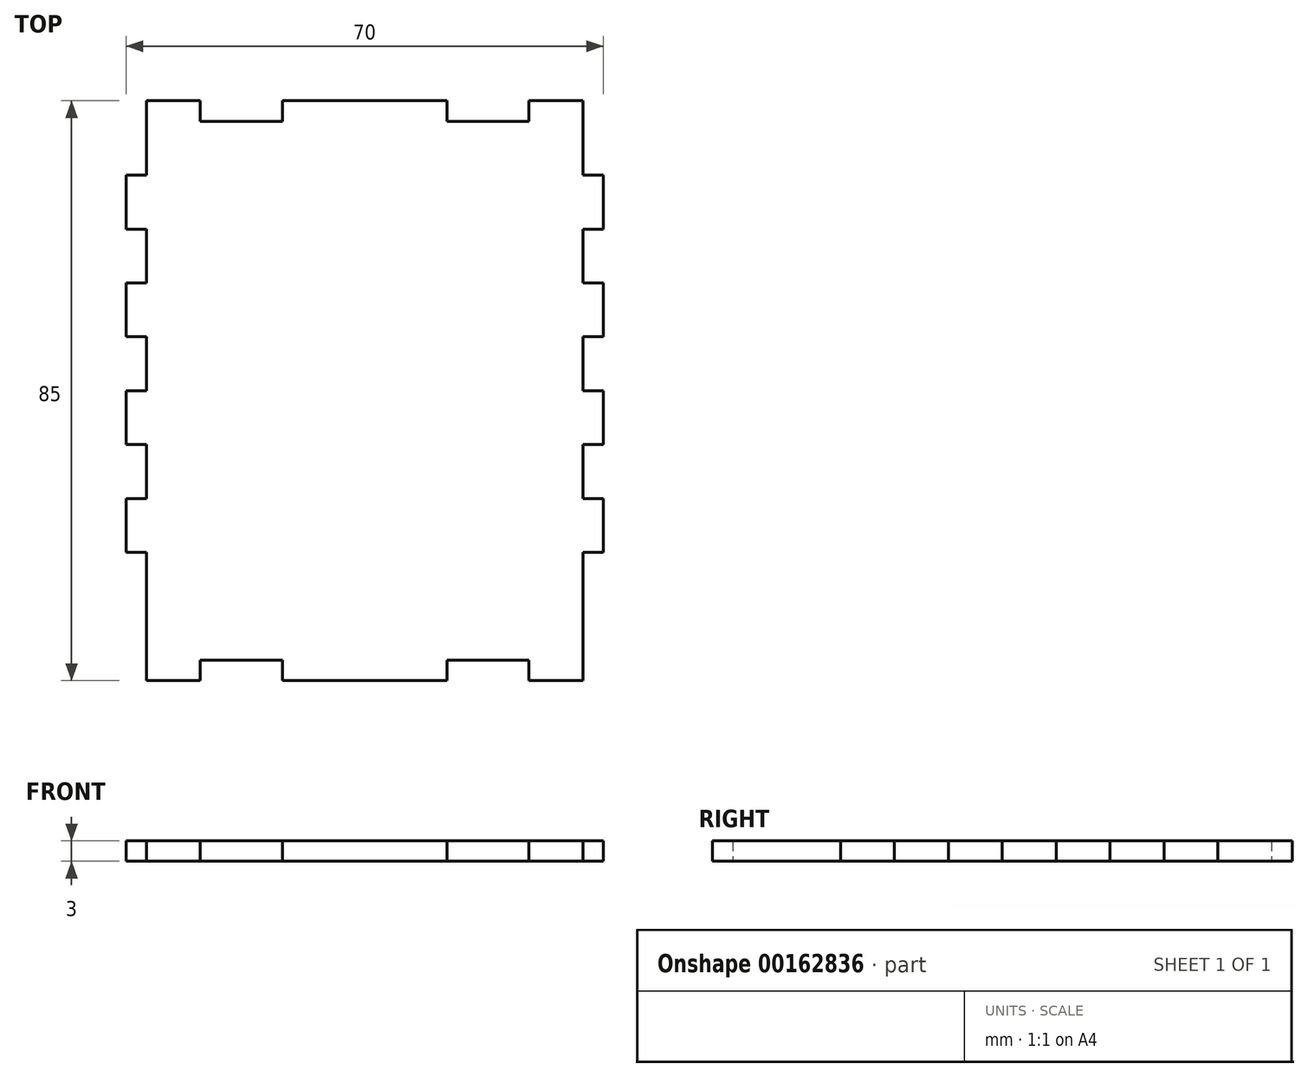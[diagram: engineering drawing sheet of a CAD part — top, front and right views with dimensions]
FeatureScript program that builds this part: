
annotation { "Feature Type Name" : "Feature", "Feature Type Description" : "" }
export const myFeature = defineFeature(function(context is Context, id is Id, definition is map)
    precondition{}
    {
        {
            var Q0;
            Q0=qCreatedBy(makeId("Top.planeOp"),FACE);
            var sketch = newSketch(context, id + "F0", { "sketchPlane" : qUnion([Q0])});
            skLineSegment(sketch, "E0.top", {"start": v(-32, -42.5) * mm, "end": v(-24.1, -42.5) * mm});
            skLineSegment(sketch, "E0.left", {"start": v(-35, 31.6) * mm, "end": v(-35, 23.7) * mm});
            skLineSegment(sketch, "E1.top", {"start": v(-24.1, -39.5) * mm, "end": v(-12.05, -39.5) * mm});
            skLineSegment(sketch, "E1.left", {"start": v(-32, 39.5) * mm, "end": v(-32, 31.6) * mm});
            skLineSegment(sketch, "E2", {"start": v(-24.1, -39.5) * mm, "end": v(-24.1, -42.5) * mm});
            skLineSegment(sketch, "E3", {"start": v(-12.05, -39.5) * mm, "end": v(-12.05, -42.5) * mm});
            skLineSegment(sketch, "E4", {"start": v(24.1, -39.5) * mm, "end": v(24.1, -42.5) * mm});
            skLineSegment(sketch, "E5", {"start": v(12.05, -39.5) * mm, "end": v(12.05, -42.5) * mm});
            skLineSegment(sketch, "E6.trimOffspring", {"start": v(-12.05, -42.5) * mm, "end": v(12.05, -42.5) * mm});
            skLineSegment(sketch, "E7.trimOffspring", {"start": v(24.1, -42.5) * mm, "end": v(32, -42.5) * mm});
            skLineSegment(sketch, "E8.trimOffspring", {"start": v(12.05, -39.5) * mm, "end": v(24.1, -39.5) * mm});
            skLineSegment(sketch, "E9", {"start": v(-32, -39.5) * mm, "end": v(-32, -42.5) * mm});
            skLineSegment(sketch, "E10", {"start": v(-35, -23.7) * mm, "end": v(-32, -23.7) * mm});
            skPoint(sketch, "E11.orphan", {"position": v(-35, -42.5) * mm});
            skLineSegment(sketch, "E12", {"start": v(-35, -15.8) * mm, "end": v(-32, -15.8) * mm});
            skLineSegment(sketch, "E13", {"start": v(-35, -7.9) * mm, "end": v(-32, -7.9) * mm});
            skLineSegment(sketch, "E14", {"start": v(-35, 0) * mm, "end": v(-32, 0) * mm});
            skLineSegment(sketch, "E15", {"start": v(-35, 7.9) * mm, "end": v(-32, 7.9) * mm});
            skLineSegment(sketch, "E16", {"start": v(-35, 15.8) * mm, "end": v(-32, 15.8) * mm});
            skLineSegment(sketch, "E17", {"start": v(-35, 23.7) * mm, "end": v(-32, 23.7) * mm});
            skLineSegment(sketch, "E18", {"start": v(-35, 31.6) * mm, "end": v(-32, 31.6) * mm});
            skLineSegment(sketch, "E19.trimOffspring", {"start": v(-35, -15.8) * mm, "end": v(-35, -23.7) * mm});
            skLineSegment(sketch, "E20.trimOffspring", {"start": v(-35, 0) * mm, "end": v(-35, -7.9) * mm});
            skLineSegment(sketch, "E21.trimOffspring", {"start": v(-35, 15.8) * mm, "end": v(-35, 7.9) * mm});
            skLineSegment(sketch, "E22", {"start": v(-32, 39.5) * mm, "end": v(-32, 42.5) * mm});
            skLineSegment(sketch, "E23.MirrorCS", {"start": v(12.05, 39.5) * mm, "end": v(12.05, 42.5) * mm});
            skLineSegment(sketch, "E24.MirrorCS", {"start": v(-12.05, 39.5) * mm, "end": v(-12.05, 42.5) * mm});
            skLineSegment(sketch, "E25.MirrorCS", {"start": v(-24.1, 39.5) * mm, "end": v(-24.1, 42.5) * mm});
            skLineSegment(sketch, "E26.MirrorCS", {"start": v(24.1, 39.5) * mm, "end": v(24.1, 42.5) * mm});
            skLineSegment(sketch, "E27.MirrorCS", {"start": v(12.05, 39.5) * mm, "end": v(24.1, 39.5) * mm});
            skLineSegment(sketch, "E28.MirrorCS", {"start": v(24.1, 42.5) * mm, "end": v(32, 42.5) * mm});
            skLineSegment(sketch, "E29.MirrorCS", {"start": v(-24.1, 39.5) * mm, "end": v(-12.05, 39.5) * mm});
            skPoint(sketch, "E30.MirrorP", {"position": v(-35, 42.5) * mm});
            skLineSegment(sketch, "E31.MirrorCS", {"start": v(-12.05, 42.5) * mm, "end": v(12.05, 42.5) * mm});
            skLineSegment(sketch, "E32.MirrorCS", {"start": v(-32, 42.5) * mm, "end": v(-24.1, 42.5) * mm});
            skLineSegment(sketch, "E33.trimOffspring", {"start": v(-32, 23.7) * mm, "end": v(-32, 15.8) * mm});
            skLineSegment(sketch, "E34.trimOffspring", {"start": v(-32, 7.9) * mm, "end": v(-32, 0) * mm});
            skLineSegment(sketch, "E35.trimOffspring", {"start": v(-32, -7.9) * mm, "end": v(-32, -15.8) * mm});
            skLineSegment(sketch, "E36.trimOffspring", {"start": v(-32, -23.7) * mm, "end": v(-32, -39.5) * mm});
            skLineSegment(sketch, "E37.MirrorCS", {"start": v(32, 39.5) * mm, "end": v(32, 42.5) * mm});
            skLineSegment(sketch, "E38.MirrorCS", {"start": v(35, 7.9) * mm, "end": v(32, 7.9) * mm});
            skLineSegment(sketch, "E39.MirrorCS", {"start": v(35, 23.7) * mm, "end": v(32, 23.7) * mm});
            skLineSegment(sketch, "E40.MirrorCS", {"start": v(35, -23.7) * mm, "end": v(32, -23.7) * mm});
            skLineSegment(sketch, "E41.MirrorCS", {"start": v(32, -39.5) * mm, "end": v(32, -42.5) * mm});
            skLineSegment(sketch, "E42.MirrorCS", {"start": v(35, 31.6) * mm, "end": v(32, 31.6) * mm});
            skLineSegment(sketch, "E43.MirrorCS", {"start": v(35, -15.8) * mm, "end": v(32, -15.8) * mm});
            skLineSegment(sketch, "E44.MirrorCS", {"start": v(35, 15.8) * mm, "end": v(32, 15.8) * mm});
            skLineSegment(sketch, "E45.MirrorCS", {"start": v(35, -7.9) * mm, "end": v(32, -7.9) * mm});
            skLineSegment(sketch, "E46.MirrorCS", {"start": v(32, 39.5) * mm, "end": v(32, 31.6) * mm});
            skLineSegment(sketch, "E47.MirrorCS", {"start": v(35, 0) * mm, "end": v(32, 0) * mm});
            skLineSegment(sketch, "E48.MirrorCS", {"start": v(32, -7.9) * mm, "end": v(32, -15.8) * mm});
            skLineSegment(sketch, "E49.MirrorCS", {"start": v(35, -15.8) * mm, "end": v(35, -23.7) * mm});
            skLineSegment(sketch, "E50.MirrorCS", {"start": v(35, 15.8) * mm, "end": v(35, 7.9) * mm});
            skLineSegment(sketch, "E51.MirrorCS", {"start": v(32, 23.7) * mm, "end": v(32, 15.8) * mm});
            skLineSegment(sketch, "E52.MirrorCS", {"start": v(35, 0) * mm, "end": v(35, -7.9) * mm});
            skPoint(sketch, "E53.MirrorP", {"position": v(35, -42.5) * mm});
            skLineSegment(sketch, "E54.MirrorCS", {"start": v(32, -23.7) * mm, "end": v(32, -39.5) * mm});
            skPoint(sketch, "E55.MirrorP", {"position": v(35, 42.5) * mm});
            skLineSegment(sketch, "E56.MirrorCS", {"start": v(35, 31.6) * mm, "end": v(35, 23.7) * mm});
            skLineSegment(sketch, "E57.MirrorCS", {"start": v(32, 7.9) * mm, "end": v(32, 0) * mm});
            skPoint(sketch, "E58.orphan", {"position": v(32, 39.5) * mm});
            skPoint(sketch, "E59.orphan", {"position": v(32, -39.5) * mm});
            skSolve(sketch);
        }
        {
            var Q0;
            Q0 = qSketchRegion(id + "F0", true);
            extrude(context, id + "F1", {"entities" : qUnion([Q0]), "depth" : 3 * mm});
        }
    });
